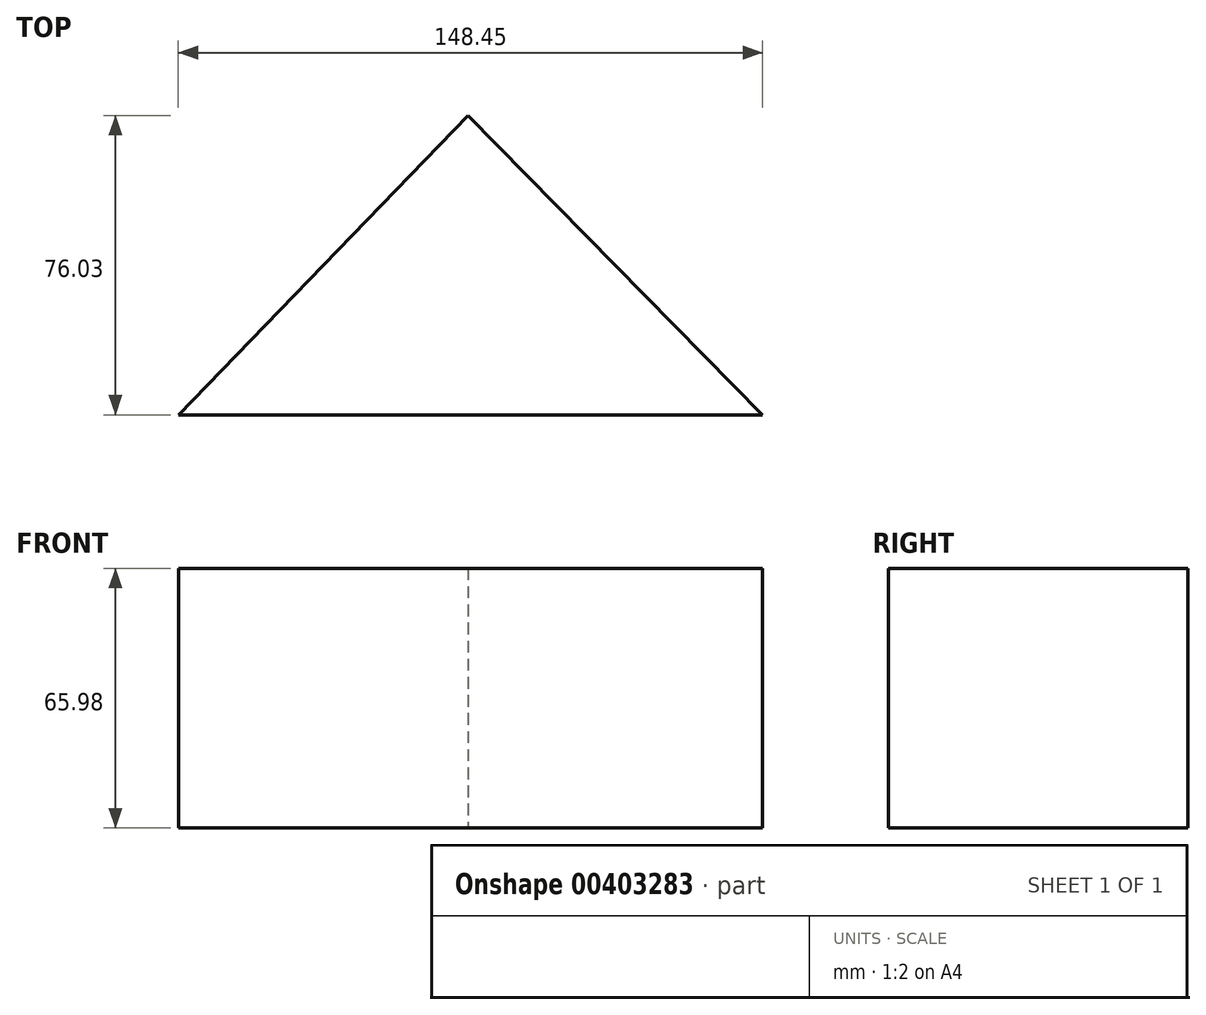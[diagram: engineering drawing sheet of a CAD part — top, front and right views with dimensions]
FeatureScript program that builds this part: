
annotation { "Feature Type Name" : "Feature", "Feature Type Description" : "" }
export const myFeature = defineFeature(function(context is Context, id is Id, definition is map)
    precondition{}
    {
        {
            var Q0;
            Q0=qCreatedBy(makeId("Top.planeOp"),FACE);
            var sketch = newSketch(context, id + "F0", { "sketchPlane" : qUnion([Q0])});
            skLineSegment(sketch, "E0", {"start": v(0, 75.51) * mm, "end": v(76.76, 75.51) * mm});
            skLineSegment(sketch, "E1", {"start": v(76.76, 75.51) * mm, "end": v(0, 0) * mm});
            skLineSegment(sketch, "E2", {"start": v(0, 0) * mm, "end": v(-73.87, 75.08) * mm});
            skLineSegment(sketch, "E3", {"start": v(-73.87, 75.08) * mm, "end": v(0, 75.51) * mm});
            skLineSegment(sketch, "E4", {"start": v(0, 0) * mm, "end": v(74.8, -76.03) * mm});
            skLineSegment(sketch, "E5", {"start": v(74.8, -76.03) * mm, "end": v(-73.65, -76.03) * mm});
            skLineSegment(sketch, "E6", {"start": v(-73.65, -76.03) * mm, "end": v(0, 0) * mm});
            skSolve(sketch);
        }
        {
            var Q0;
            Q0=makeQuery(id+"F0.imprint","IMPRINT",FACE,{"disambiguationData":[TD([[makeQuery(id+"F0.imprint","IMPRINT",EDGE,{"derivedFrom":sQuery(id+"F0.wireOp",EDGE,"E4")}),-1.0]])]});
            extrude(context, id + "F1", {"entities" : qUnion([Q0]), "depth" : 65.98 * mm});
        }
    });
